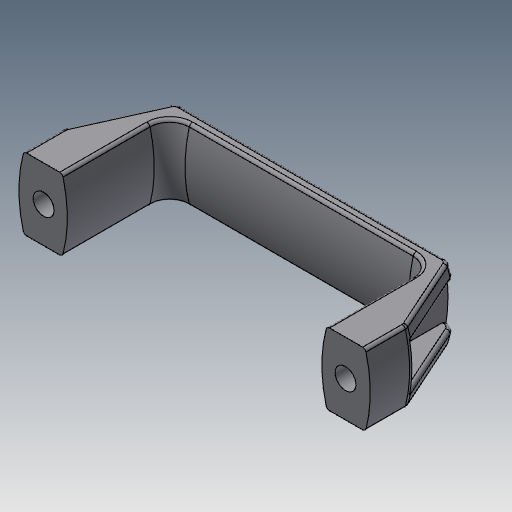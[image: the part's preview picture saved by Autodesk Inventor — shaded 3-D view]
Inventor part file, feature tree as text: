
AUTODESK INVENTOR PART (.ipt)
format: ipt  version: 2018.3 (Build 223284000, 284)  size: 235,008 bytes
history: native  units: in
note: dims shown in document units (in); Inventor stores cm internally (conversion verified against a paired STEP export)
features: sketch x1, fillet x1
ambient origin geometry x8: Origin, YZ Plane, XZ Plane, XY Plane, X Axis, Y Axis, Z Axis, Center Point
bodies: Solid1 (feature_tree)
feature tree (2):
  sketch  "Sketch1"
  fillet  "Fillet1"  Radius=3.6875in
